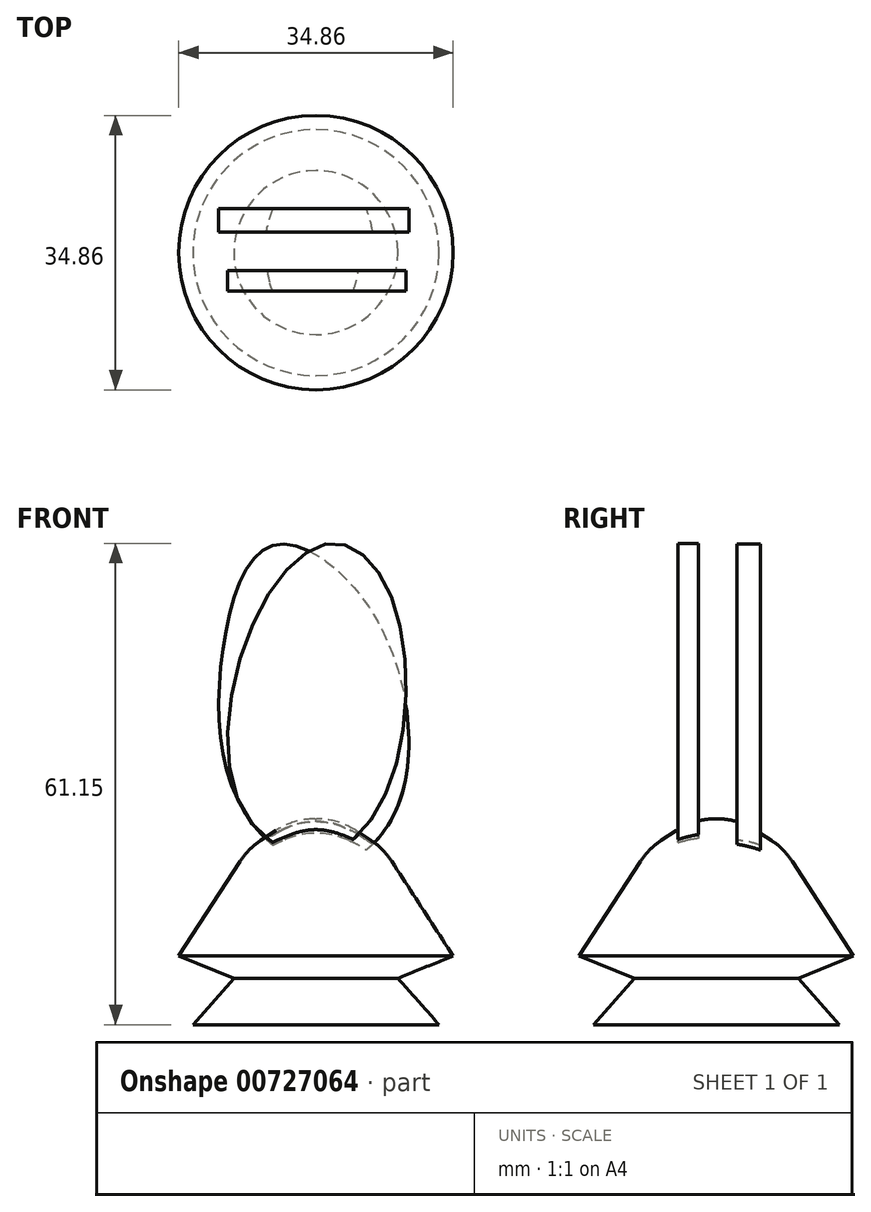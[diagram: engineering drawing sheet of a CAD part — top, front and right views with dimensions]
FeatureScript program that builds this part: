
annotation { "Feature Type Name" : "Feature", "Feature Type Description" : "" }
export const myFeature = defineFeature(function(context is Context, id is Id, definition is map)
    precondition{}
    {
        {
            var Q0;
            Q0=qCreatedBy(makeId("Front.planeOp"),FACE);
            var sketch = newSketch(context, id + "F0", { "sketchPlane" : qUnion([Q0])});
            skLineSegment(sketch, "E0", {"start": v(0, 0) * mm, "end": v(-15.63, 0) * mm});
            skLineSegment(sketch, "E1", {"start": v(-15.63, 0) * mm, "end": v(-10.42, 5.91) * mm});
            skLineSegment(sketch, "E2", {"start": v(-10.42, 5.91) * mm, "end": v(-17.43, 8.72) * mm});
            skLineSegment(sketch, "E3", {"start": v(-17.43, 8.72) * mm, "end": v(-8.62, 22.34) * mm});
            skLineSegment(sketch, "E4", {"start": v(-8.62, 22.34) * mm, "end": v(-2.8, 26.15) * mm});
            skLineSegment(sketch, "E5", {"start": v(-2.8, 26.15) * mm, "end": v(0, 26.15) * mm});
            skLineSegment(sketch, "E6", {"start": v(0, 26.15) * mm, "end": v(0, 0) * mm});
            skSolve(sketch);
        }
        {
            var Q0;
            Q0 = qSketchRegion(id + "F0", true);
            var Q1;
            Q1=sQuery(id+"F0.wireOp",EDGE,"E6");
            revolve(context, id + "F1", {"surfaceOperationType" : NewSurfaceOperationType.NEW, "entities" : qUnion([Q0]), "axis" : qUnion([Q1]), "revolveType" : RevolveType.FULL});
        }
        {
            var Q0;
            Q0=makeQuery(id+"F1.opRevolve","SWEPT_FACE",FACE,{"disambiguationData":[OSD([sQuery(id+"F0.wireOp",EDGE,"E4")])]});
            fillet(context, id + "F2", {"entities" : qUnion([Q0]), "radius" : 9.06 * mm, "tangentPropagation" : true, "allowEdgeOverflow" : false});
        }
        {
            var Q0;
            Q0=qCreatedBy(makeId("Front.planeOp"),FACE);
            cPlane(context, id + "F3", {"entities" : qUnion([Q0]), "cplaneType" : CPlaneType.OFFSET, "offset" : 3.6 * mm, "width" : 150 * mm, "height" : 150 * mm});
        }
        {
            var Q0;
            Q0=qCreatedBy(id+"F3.planeOp",FACE);
            var sketch = newSketch(context, id + "F4", { "sketchPlane" : qUnion([Q0])});
            skFitSpline(sketch, "E7", {"points": [v(2.2, 61.15) * mm, v(-7.43, 52.14) * mm, v(-9.63, 27.89) * mm, v(0.99, 21.68) * mm, v(10, 32.5) * mm, v(9.4, 54.74) * mm, v(2.2, 61.15) * mm]});
            skSolve(sketch);
        }
        {
            var Q0;
            Q0=makeQuery(id+"F4.imprint","IMPRINT",FACE,{"disambiguationData":[TD([[makeQuery(id+"F4.imprint","IMPRINT",EDGE,{"derivedFrom":sQuery(id+"F4.wireOp",EDGE,"E7")}),1.0]])]});
            extrude(context, id + "F5", {"entities" : qUnion([Q0]), "operationType" : NewBodyOperationType.ADD, "endBound" : BoundingType.SYMMETRIC, "depth" : 2.6 * mm, "offsetDistance" : 25 * mm});
        }
        {
            var Q0;
            Q0=qCreatedBy(makeId("Front.planeOp"),FACE);
            cPlane(context, id + "F6", {"entities" : qUnion([Q0]), "cplaneType" : CPlaneType.OFFSET, "offset" : 4.1 * mm, "oppositeDirection" : true, "width" : 150 * mm, "height" : 150 * mm});
        }
        {
            var Q0;
            Q0=qCreatedBy(id+"F6.planeOp",FACE);
            var sketch = newSketch(context, id + "F7", { "sketchPlane" : qUnion([Q0])});
            skFitSpline(sketch, "E8", {"points": [v(-5.61, 60.82) * mm, v(7.01, 52.6) * mm, v(10.62, 28.35) * mm, v(1, 20.14) * mm, v(-9.62, 27.95) * mm, v(-11.82, 47.6) * mm, v(-5.61, 60.82) * mm]});
            skSolve(sketch);
        }
        {
            var Q0;
            Q0=makeQuery(id+"F7.imprint","IMPRINT",FACE,{"disambiguationData":[TD([[makeQuery(id+"F7.imprint","IMPRINT",EDGE,{"derivedFrom":sQuery(id+"F7.wireOp",EDGE,"E8")}),-1.0]])]});
            extrude(context, id + "F8", {"entities" : qUnion([Q0]), "operationType" : NewBodyOperationType.ADD, "endBound" : BoundingType.SYMMETRIC, "depth" : 3 * mm, "offsetDistance" : 25 * mm});
        }
    });
